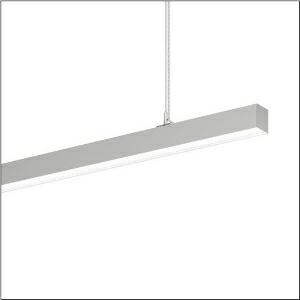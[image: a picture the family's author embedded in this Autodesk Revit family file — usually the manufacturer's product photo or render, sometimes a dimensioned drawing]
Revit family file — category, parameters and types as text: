
# Revit family: silica_r__21_51mx30da34sb_350b
name_source: partatom
category: Lighting Fixtures
units: mm (PartAtom-declared; Revit-internal decimal feet)

## family parameters
Cut with Voids When Loaded = No
Host = Face
Light Source = No
Part Type = Normal
Room Calculation Point = No
Round Connector Dimension = Use Diameter
Shared = No

## types (1)
- --- (1 x LED, 4210 lm, 27.7 W, 3000K)
    Apparent Load = 28 VA
    CIE Flux Codes = 47 79 96 57 100
    Color Rendering = 80
    Color Temperature = 3000K
    Default Elevation = 1800 mm
    Description = Silica® 21, office luminaire, primary optical cover: cover, of PMMA, opal, light emission: direct/indirect distribution, primary light characteristic: symmetric, installation type: suspended mounting, LED, rated luminous flux: 4.210lm, luminous efficacy: 152lm/W, light colour: 830, colour temperature: 3000K, control gear: DALI 2, with terminal, 3+2-pole, max. 2.5mm², mains connection: 220..240V, AC, 50/60Hz, rated input power: 27.7W, luminaire housing, of aluminium, metallic grey (RAL 9006), length: 1.204mm, width: 53mm, height: 53mm, protection rating (complete): IP20, insulation class (complete): insulation class I (protective earthing), certification: CE, permissible operating ambient temperature: 0..+35°C, standard: EN 50419, packaging unit: 1 piece
    Height = 53 mm
    Lamp = 1 x LED
    Lamp Light Flux = 4210 lm
    Lamp Power = 27.7 W
    Lamp count = 1
    Length = 1204 mm
    Luminous efficacy = 152 lm/W
    Manufacturer = Siteco
    ModVariant = No
    Model = 51MX30DA34SB
    Mounting Place = Ceiling
    Mounting Type = Pendant
    Number of Poles = 1
    OnlyDefault = Yes
    Power Factor = 1
    Product Name = Silica® 21
    Product group = office luminaire | ceiling pendant
    ProductGroupID = 903
    Protection Class = Protection class I
    Protection Degree = IP 20
    RLX_Detail_Level = 1
    RLX_Emergency_Light_Flux = 0 lm
    RLX_Emergency_Type = 0
    RLX_Emergency_Type_DB = No
    RlxData = <blob elided: 23305 chars, md5=7a249cc8>
    Socket = socket
    Standby Power = 0 W
    System Light Flux = 4210 lm
    System Power = 28 W
    Type Comments = factory setting: luminous flux: 100 % | dim-lin: 254 | 233 mA
    Type Image = l_1335864.jpg
    URL = http://relux.com
    VarID = @adj_138667
    Voltage = 0 V
    Weight = 0.00 kg
    Width = 53 mm

## geometry (parser evidence)
native form markers: Blend x4, Sweep x12
no freeform markers — native parametric forms only
